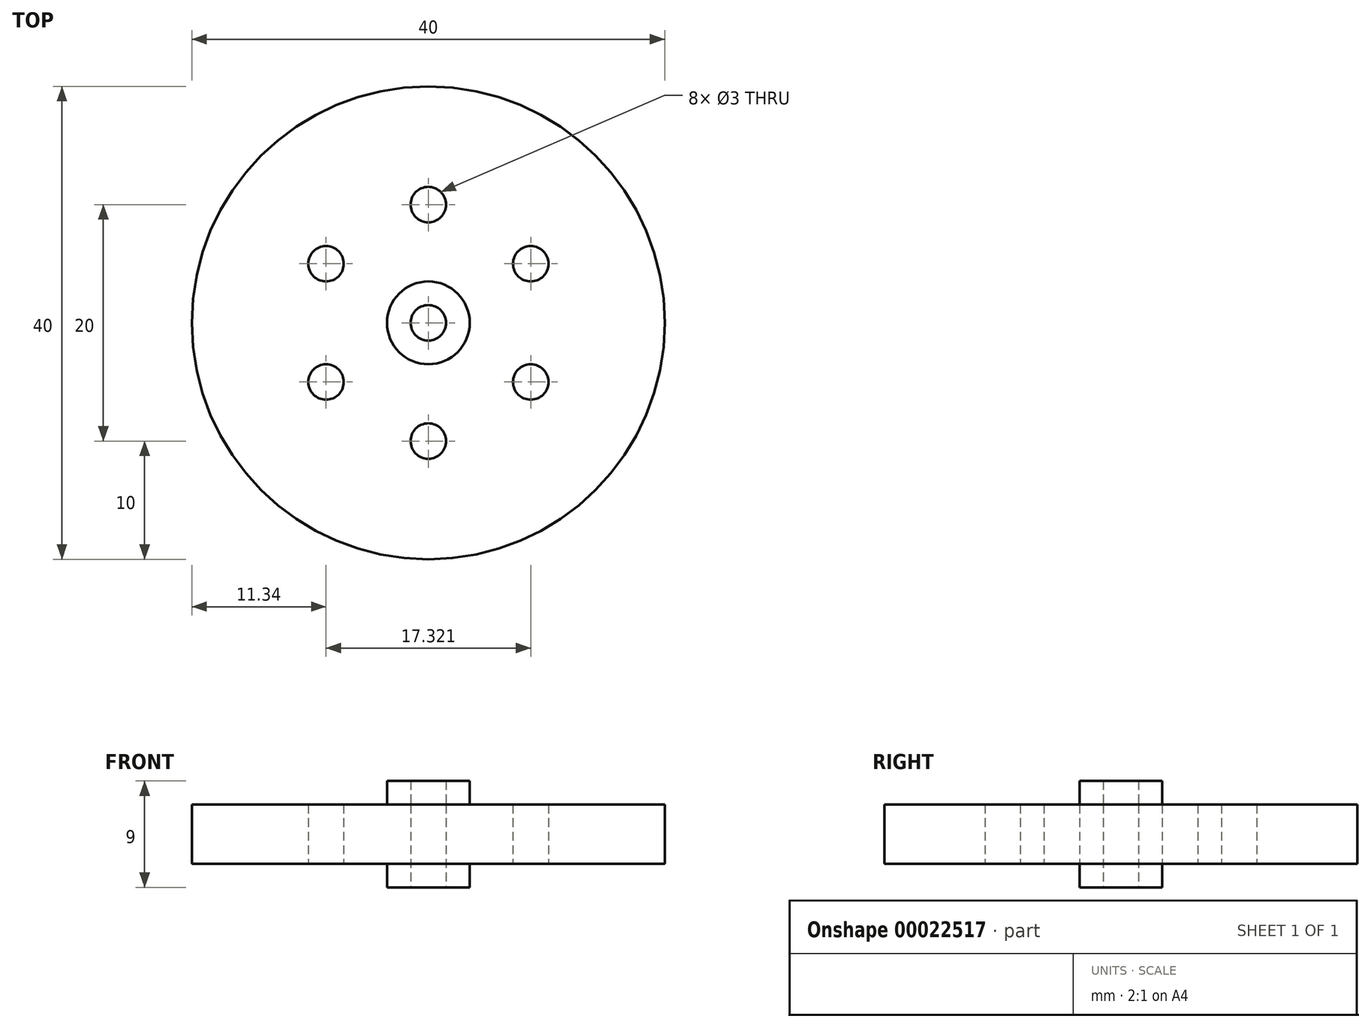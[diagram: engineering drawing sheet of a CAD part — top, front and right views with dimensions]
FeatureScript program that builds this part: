
annotation { "Feature Type Name" : "Feature", "Feature Type Description" : "" }
export const myFeature = defineFeature(function(context is Context, id is Id, definition is map)
    precondition{}
    {
        {
            var Q0;
            Q0=qCreatedBy(makeId("Top.planeOp"),FACE);
            var sketch = newSketch(context, id + "F0", { "sketchPlane" : qUnion([Q0])});
            skCircle(sketch, "E0", {"center": v(0, 0) * mm, "radius": 20 * mm});
            skLineSegment(sketch, "E1", {"start": v(0, 0) * mm, "end": v(0, 10) * mm});
            skCircle(sketch, "E2", {"center": v(0, 10) * mm, "radius": 1.5 * mm});
            skCircle(sketch, "E3.1.0", {"center": v(-8.66, 5) * mm, "radius": 1.5 * mm});
            skCircle(sketch, "E3.2.0", {"center": v(-8.66, -5) * mm, "radius": 1.5 * mm});
            skCircle(sketch, "E3.3.0", {"center": v(0, -10) * mm, "radius": 1.5 * mm});
            skCircle(sketch, "E3.4.0", {"center": v(8.66, -5) * mm, "radius": 1.5 * mm});
            skCircle(sketch, "E3.5.0", {"center": v(8.66, 5) * mm, "radius": 1.5 * mm});
            skCircle(sketch, "E4", {"center": v(0, 0) * mm, "radius": 1.5 * mm});
            skSolve(sketch);
        }
        {
            var Q0;
            Q0=qSketchRegion(id+"F0",true);
            extrude(context, id + "F1", {"entities" : qUnion([Q0]), "depth" : 5 * mm});
        }
        {
            var Q0;
            Q0=makeQuery(id+"F1.opExtrude","SWEPT_BODY",BODY,{"disambiguationData":[OSD([sQuery(id+"F0.wireOp",EDGE,"E0")])]});
            transform(context, id + "F2", {"entities" : qUnion([Q0]), "transformType" : TransformType.TRANSLATION_3D, "dx" : 0 * mm, "dy" : 0 * mm, "dz" : 0 * mm, "makeCopy" : true});
        }
        {
            var Q0;
            Q0=makeQuery(id+"F2.opPattern","COPY",BODY,{"derivedFrom":makeQuery(id+"F1.opExtrude","SWEPT_BODY",BODY,{"disambiguationData":[OSD([sQuery(id+"F0.wireOp",EDGE,"E0")])]}),"instanceName":"1"});
            transform(context, id + "F3", {"entities" : qUnion([Q0]), "transformType" : TransformType.TRANSLATION_3D, "dx" : 0 * mm, "dy" : 0 * mm, "dz" : 0 * mm, "makeCopy" : true});
        }
        {
            var Q0;
            Q0=makeQuery(id+"F3.opPattern","COPY",FACE,{"derivedFrom":makeQuery(id+"F2.opPattern","COPY",FACE,{"derivedFrom":makeQuery(id+"F1.opExtrude","CAP_FACE",FACE,{"disambiguationData":[OSD([sQuery(id+"F0.wireOp",EDGE,"E0"),sQuery(id+"F0.wireOp",EDGE,"E2"),sQuery(id+"F0.wireOp",EDGE,"E3.1.0"),sQuery(id+"F0.wireOp",EDGE,"E3.2.0"),sQuery(id+"F0.wireOp",EDGE,"E3.3.0"),sQuery(id+"F0.wireOp",EDGE,"E3.4.0"),sQuery(id+"F0.wireOp",EDGE,"E3.5.0")])],"isStart":false}),"instanceName":"1"}),"instanceName":"1"});
            var sketch = newSketch(context, id + "F4", { "sketchPlane" : qUnion([Q0])});
            skSolve(sketch);
        }
        {
            var Q0;
            Q0=makeQuery(id+"F4.imprint","IMPRINT",FACE,{"disambiguationData":[TD([[makeQuery(id+"F4.imprint","IMPRINT",EDGE,{"derivedFrom":makeQuery(id+"F3.opPattern","COPY",EDGE,{"derivedFrom":makeQuery(id+"F2.opPattern","COPY",EDGE,{"derivedFrom":makeQuery(id+"F1.opExtrude","CAP_EDGE",EDGE,{"disambiguationData":[OSD([sQuery(id+"F0.wireOp",EDGE,"E0")])],"isStart":false}),"instanceName":"1"}),"instanceName":"1"})}),1.0]])]});
            var sketch = newSketch(context, id + "F5", { "sketchPlane" : qUnion([Q0])});
            skCircle(sketch, "E5", {"center": v(0, 0) * mm, "radius": 3.5 * mm});
            skSolve(sketch);
        }
        {
            var Q0;
            Q0=makeQuery(id+"F5.imprint","IMPRINT",FACE,{"disambiguationData":[TD([[makeQuery(id+"F5.imprint","IMPRINT",EDGE,{"derivedFrom":sQuery(id+"F5.wireOp",EDGE,"E5")}),1.0]])]});
            var Q1;
            Q1=sQuery(id+"F0.wireOp",EDGE,"E4");
            var Q2;
            Q2=sQuery(id+"F5.wireOp",EDGE,"E5");
            extrude(context, id + "F6", {"entities" : qUnion([Q0]), "surfaceEntities" : qUnion([Q1, Q2]), "depth" : 2 * mm});
        }
        {
            var Q0;
            Q0=makeQuery(id+"F0.imprint","IMPRINT",FACE,{"disambiguationData":[TD([[makeQuery(id+"F0.imprint","IMPRINT",EDGE,{"derivedFrom":sQuery(id+"F0.wireOp",EDGE,"E0")}),1.0]])]});
            var sketch = newSketch(context, id + "F7", { "sketchPlane" : qUnion([Q0])});
            skCircle(sketch, "E6", {"center": v(0, 0) * mm, "radius": 3.5 * mm});
            skSolve(sketch);
        }
        {
            var Q0;
            Q0=makeQuery(id+"F7.imprint","IMPRINT",FACE,{"disambiguationData":[TD([[makeQuery(id+"F7.imprint","IMPRINT",EDGE,{"derivedFrom":sQuery(id+"F7.wireOp",EDGE,"E6")}),1.0]])]});
            var Q1;
            Q1=sQuery(id+"F7.wireOp",EDGE,"E6");
            extrude(context, id + "F8", {"entities" : qUnion([Q0]), "operationType" : NewBodyOperationType.ADD, "surfaceEntities" : qUnion([Q1]), "oppositeDirection" : true, "depth" : 2 * mm});
        }
    });
